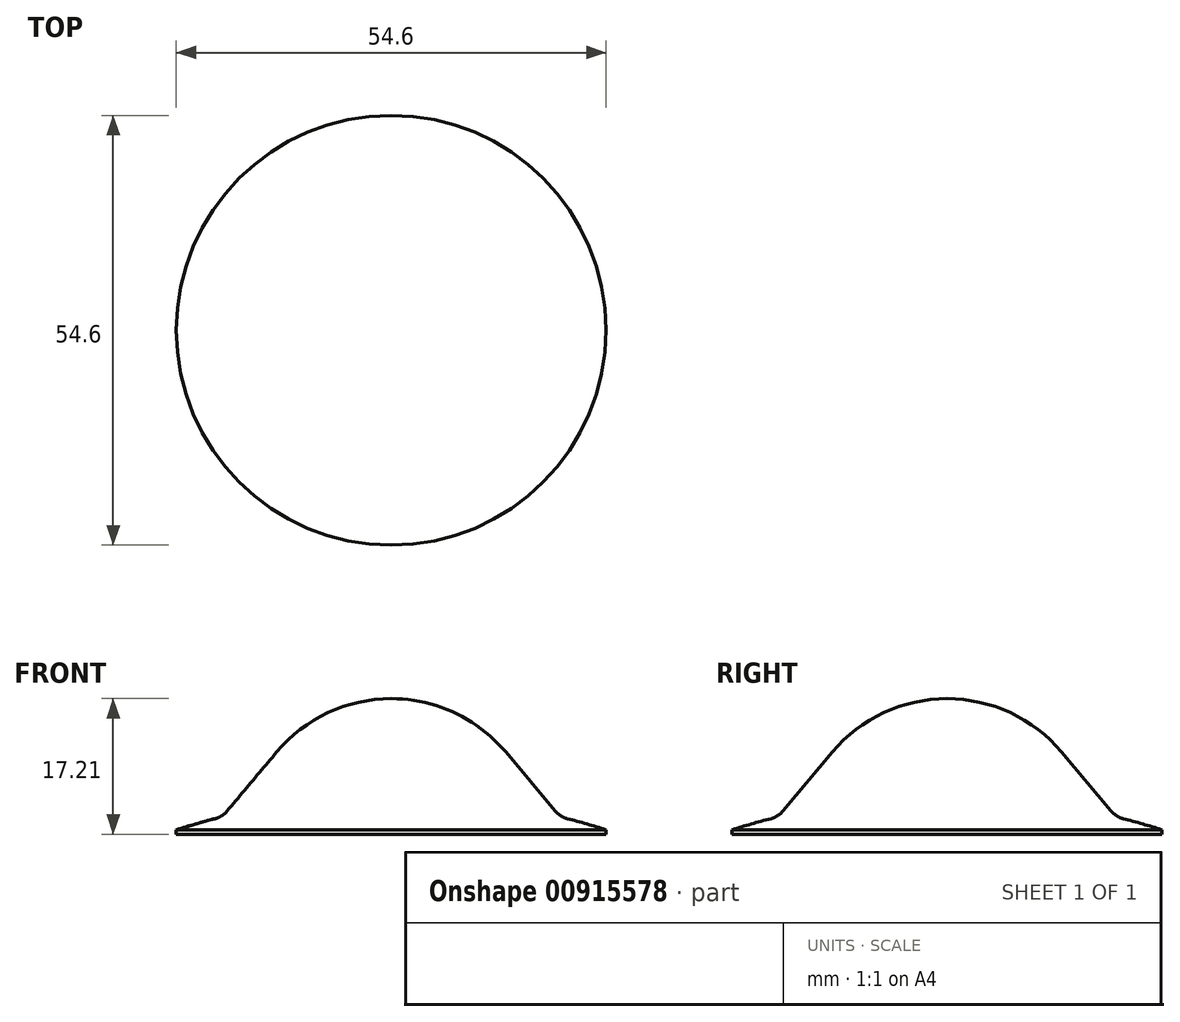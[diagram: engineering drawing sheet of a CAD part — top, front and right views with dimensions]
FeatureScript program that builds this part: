
annotation { "Feature Type Name" : "Feature", "Feature Type Description" : "" }
export const myFeature = defineFeature(function(context is Context, id is Id, definition is map)
    precondition{}
    {
        {
            var Q0;
            Q0=qCreatedBy(makeId("Front.planeOp"),FACE);
            var sketch = newSketch(context, id + "F0", { "sketchPlane" : qUnion([Q0])});
            skArc(sketch, "E0", {"start": v(14.55, 12.21) * mm, "mid": v(0, 19) * mm, "end": v(-14.55, 12.21) * mm});
            skLineSegment(sketch, "E1.bottom", {"start": v(-27.3, 2.34) * mm, "end": v(27.3, 2.34) * mm});
            skLineSegment(sketch, "E1.top", {"start": v(-27.3, 1.79) * mm, "end": v(27.3, 1.79) * mm});
            skLineSegment(sketch, "E1.left", {"start": v(-27.3, 2.34) * mm, "end": v(-27.3, 1.79) * mm});
            skLineSegment(sketch, "E1.right", {"start": v(27.3, 2.34) * mm, "end": v(27.3, 1.79) * mm});
            skLineSegment(sketch, "E2", {"start": v(0, 0) * mm, "end": v(0, -50.6) * mm});
            skArc(sketch, "E3", {"start": v(27.3, 2.34) * mm, "mid": v(24.85, 3.08) * mm, "end": v(22.39, 3.75) * mm});
            skArc(sketch, "E4.trimOffspring", {"start": v(-18.86, 2.34) * mm, "mid": v(-18.89, 2.07) * mm, "end": v(-18.92, 1.79) * mm});
            skArc(sketch, "E5.trimOffspring", {"start": v(-22.39, 3.75) * mm, "mid": v(-24.85, 3.08) * mm, "end": v(-27.3, 2.34) * mm});
            skLineSegment(sketch, "E6", {"start": v(14.55, 12.21) * mm, "end": v(20.83, 4.73) * mm});
            skLineSegment(sketch, "E7", {"start": v(-14.55, 12.21) * mm, "end": v(-20.83, 4.73) * mm});
            skPoint(sketch, "E8.visualSharp", {"position": v(-21.46, 3.98) * mm});
            skArc(sketch, "E8.filletArc", {"start": v(-22.39, 3.75) * mm, "mid": v(-21.53, 4.12) * mm, "end": v(-20.83, 4.73) * mm});
            skPoint(sketch, "E9.visualSharp", {"position": v(21.46, 3.98) * mm});
            skArc(sketch, "E9.filletArc", {"start": v(20.83, 4.73) * mm, "mid": v(21.53, 4.12) * mm, "end": v(22.39, 3.75) * mm});
            skLineSegment(sketch, "E10", {"start": v(0, 0) * mm, "end": v(0, 28.38) * mm});
            skSolve(sketch);
        }
        {
            var Q0;
            {var subQ5=sQuery(id+"F0.wireOp",EDGE,"E5.trimOffspring");Q0=makeQuery(id+"F0.imprint","IMPRINT",FACE,{"disambiguationData":[TD([[makeQuery(id+"F0.imprint","IMPRINT",EDGE,{"derivedFrom":subQ5}),1.0]])]});}
            var Q1;
            {var subQ0=sQuery(id+"F0.wireOp",EDGE,"E4.trimOffspring");Q1=makeQuery(id+"F0.imprint","IMPRINT",FACE,{"disambiguationData":[TD([[makeQuery(id+"F0.imprint","IMPRINT",EDGE,{"derivedFrom":subQ0}),1.0]])]});}
            var Q2;
            {var subQ0=sQuery(id+"F0.wireOp",EDGE,"E1.left");Q2=makeQuery(id+"F0.imprint","IMPRINT",FACE,{"disambiguationData":[TD([[makeQuery(id+"F0.imprint","IMPRINT",EDGE,{"derivedFrom":subQ0}),1.0]])]});}
            var Q3;
            Q3=sQuery(id+"F0.wireOp",EDGE,"E10");
            revolve(context, id + "F1", {"surfaceOperationType" : NewSurfaceOperationType.NEW, "entities" : qUnion([Q0, Q1, Q2]), "axis" : qUnion([Q3]), "revolveType" : RevolveType.FULL});
        }
    });
